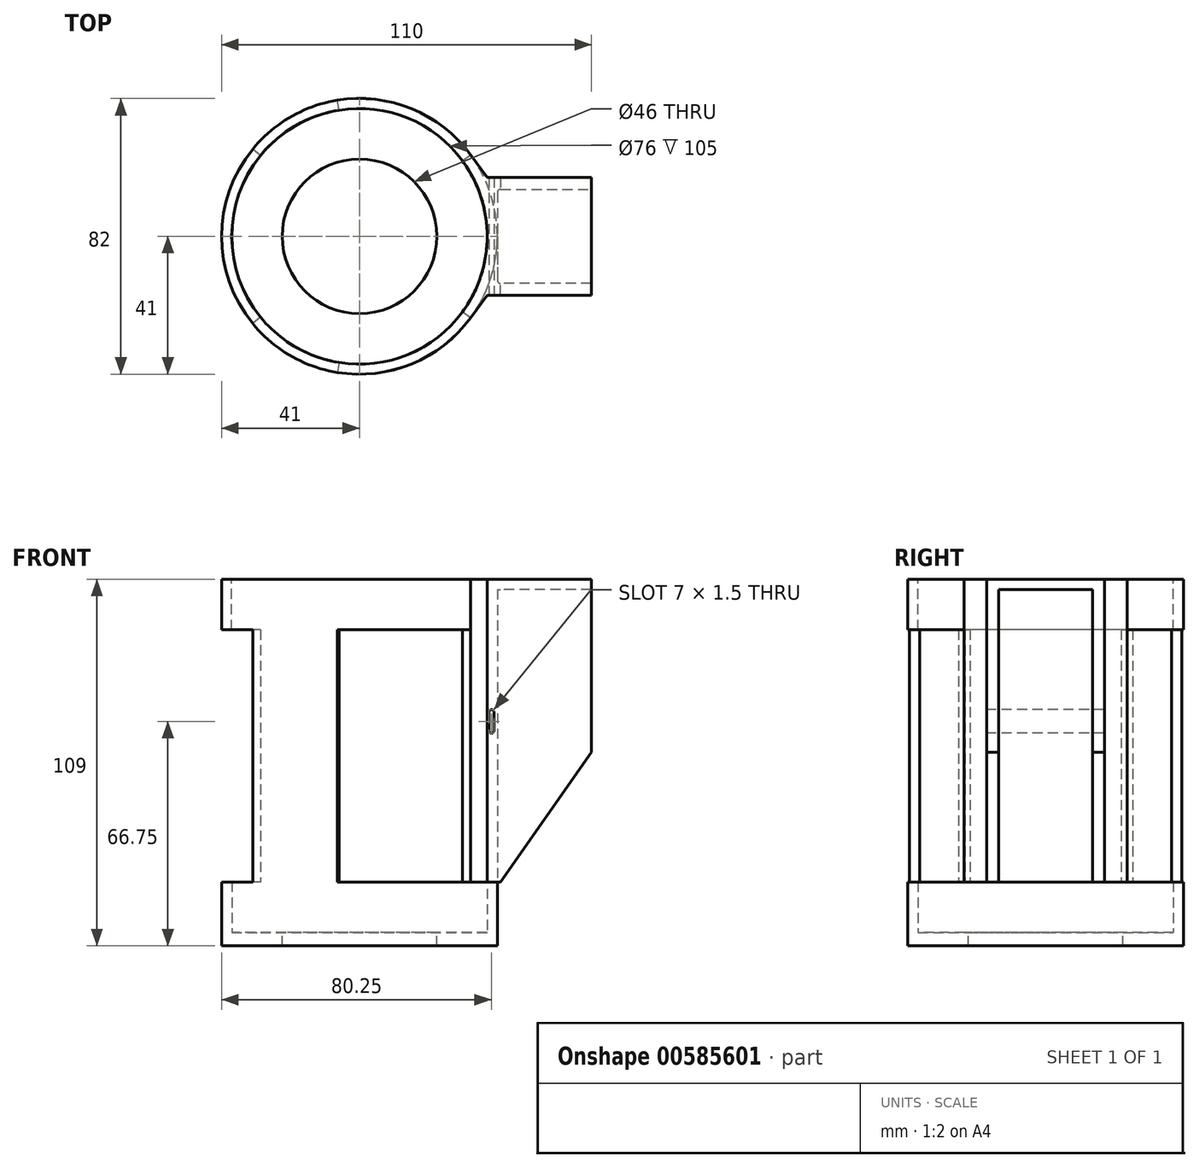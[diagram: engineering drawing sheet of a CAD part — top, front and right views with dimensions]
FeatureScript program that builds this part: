
annotation { "Feature Type Name" : "Feature", "Feature Type Description" : "" }
export const myFeature = defineFeature(function(context is Context, id is Id, definition is map)
    precondition{}
    {
        {
            var Q0;
            Q0=qCreatedBy(makeId("Top.planeOp"),FACE);
            var sketch = newSketch(context, id + "F0", { "sketchPlane" : qUnion([Q0])});
            skCircle(sketch, "E0", {"center": v(0, 0) * mm, "radius": 41 * mm});
            skCircle(sketch, "E1", {"center": v(0, 0) * mm, "radius": 23 * mm});
            skCircle(sketch, "E2", {"center": v(0, 0) * mm, "radius": 38 * mm});
            skSolve(sketch);
        }
        {
            var Q0;
            Q0=makeQuery(id+"F0.imprint","IMPRINT",FACE,{"disambiguationData":[TD([[makeQuery(id+"F0.imprint","IMPRINT",EDGE,{"derivedFrom":sQuery(id+"F0.wireOp",EDGE,"E1")}),-1.0]])]});
            var Q1;
            Q1=makeQuery(id+"F0.imprint","IMPRINT",FACE,{"disambiguationData":[TD([[makeQuery(id+"F0.imprint","IMPRINT",EDGE,{"derivedFrom":sQuery(id+"F0.wireOp",EDGE,"E0")}),1.0]])]});
            extrude(context, id + "F1", {"entities" : qUnion([Q0, Q1]), "oppositeDirection" : true, "depth" : 4 * mm, "offsetDistance" : 25 * mm});
        }
        {
            var Q0;
            Q0=makeQuery(id+"F0.imprint","IMPRINT",FACE,{"disambiguationData":[TD([[makeQuery(id+"F0.imprint","IMPRINT",EDGE,{"derivedFrom":sQuery(id+"F0.wireOp",EDGE,"E0")}),1.0]])]});
            extrude(context, id + "F2", {"entities" : qUnion([Q0]), "operationType" : NewBodyOperationType.ADD, "depth" : 15 * mm, "offsetDistance" : 25 * mm});
        }
        {
            var Q0;
            Q0=makeQuery(id+"F2.opExtrude","CAP_FACE",FACE,{"disambiguationData":[OSD([sQuery(id+"F0.wireOp",EDGE,"E0"),sQuery(id+"F0.wireOp",EDGE,"E2")])],"isStart":false});
            var sketch = newSketch(context, id + "F3", { "sketchPlane" : qUnion([Q0])});
            skLineSegment(sketch, "E3", {"start": v(38, 17.5) * mm, "end": v(0, 0) * mm});
            skLineSegment(sketch, "E4.MirrorCS", {"start": v(38, -17.5) * mm, "end": v(0, 0) * mm});
            skLineSegment(sketch, "E5", {"start": v(38, 17.5) * mm, "end": v(69, 17.5) * mm});
            skLineSegment(sketch, "E6", {"start": v(38, -17.5) * mm, "end": v(69, -17.5) * mm});
            skPoint(sketch, "E7.startSnap0", {"position": v(69, 0) * mm});
            skLineSegment(sketch, "E8", {"start": v(0, 0) * mm, "end": v(-8.31, 51.05) * mm});
            skLineSegment(sketch, "E9.MirrorCS", {"start": v(0, 0) * mm, "end": v(-40.06, 32.72) * mm});
            skLineSegment(sketch, "E10.MirrorCS", {"start": v(0, 0) * mm, "end": v(-8.31, -51.05) * mm});
            skLineSegment(sketch, "E11.MirrorCS", {"start": v(0, 0) * mm, "end": v(-40.06, -32.72) * mm});
            skPoint(sketch, "E12.visualSharp", {"position": v(41, -14) * mm});
            skPoint(sketch, "E13", {"position": v(41, 14) * mm});
            skPoint(sketch, "E14", {"position": v(69, -14) * mm});
            skPoint(sketch, "E15", {"position": v(69, 14) * mm});
            skLineSegment(sketch, "E16", {"start": v(69, -14) * mm, "end": v(42, -14) * mm});
            skLineSegment(sketch, "E17", {"start": v(41, 13) * mm, "end": v(41, -13) * mm});
            skLineSegment(sketch, "E18", {"start": v(42, 14) * mm, "end": v(69, 14) * mm});
            skLineSegment(sketch, "E19", {"start": v(69, -17.5) * mm, "end": v(69, 17.5) * mm});
            skArc(sketch, "E20.filletArc", {"start": v(41, -13) * mm, "mid": v(41.3, -13.7) * mm, "end": v(42, -14) * mm});
            skArc(sketch, "E21.filletArc", {"start": v(42, 14) * mm, "mid": v(41.3, 13.7) * mm, "end": v(41, 13) * mm});
            skLineSegment(sketch, "E22", {"start": v(38, -17.5) * mm, "end": v(33.09, -24.22) * mm});
            skLineSegment(sketch, "E23", {"start": v(38, 17.5) * mm, "end": v(33.09, 24.22) * mm});
            skLineSegment(sketch, "E24", {"start": v(33.09, -24.22) * mm, "end": v(0, 0) * mm});
            skLineSegment(sketch, "E25", {"start": v(0, 0) * mm, "end": v(33.09, 24.22) * mm});
            skSolve(sketch);
        }
        {
            var Q0;
            {var subQ0=sQuery(id+"F3.wireOp",EDGE,"E22");Q0=makeQuery(id+"F3.imprint","IMPRINT",FACE,{"disambiguationData":[TD([[makeQuery(id+"F3.imprint","IMPRINT",EDGE,{"derivedFrom":subQ0}),-1.0]])]});}
            var Q1;
            {var subQ1=sQuery(id+"F3.wireOp",EDGE,"E4.MirrorCS");var subQ3=makeQuery(id+"F2.opExtrude","CAP_EDGE",EDGE,{"disambiguationData":[OSD([sQuery(id+"F0.wireOp",EDGE,"E0")])],"isStart":false});var subQ4=makeQuery(id+"F3.imprint","INTERSECT",VERTEX,{"derivedFrom":[subQ3,subQ1]});Q1=makeQuery(id+"F3.imprint","IMPRINT",FACE,{"disambiguationData":[TD([[makeQuery(id+"F3.imprint","IMPRINT",EDGE,{"disambiguationData":[TD([[subQ4,-1.0]])],"derivedFrom":subQ3}),-1.0]])]});}
            var Q2;
            {var subQ0=sQuery(id+"F3.wireOp",EDGE,"E4.MirrorCS");var subQ1=makeQuery(id+"F2.opExtrude","CAP_EDGE",EDGE,{"disambiguationData":[OSD([sQuery(id+"F0.wireOp",EDGE,"E0")])],"isStart":false});var subQ2=makeQuery(id+"F3.imprint","INTERSECT",VERTEX,{"derivedFrom":[subQ1,subQ0]});Q2=makeQuery(id+"F3.imprint","IMPRINT",FACE,{"disambiguationData":[TD([[makeQuery(id+"F3.imprint","IMPRINT",EDGE,{"disambiguationData":[TD([[subQ2,-1.0]])],"derivedFrom":subQ0}),-1.0]])]});}
            var Q3;
            {var subQ0=sQuery(id+"F3.wireOp",EDGE,"E4.MirrorCS");var subQ1=makeQuery(id+"F2.opExtrude","CAP_EDGE",EDGE,{"disambiguationData":[OSD([sQuery(id+"F0.wireOp",EDGE,"E0")])],"isStart":false});var subQ2=makeQuery(id+"F3.imprint","INTERSECT",VERTEX,{"derivedFrom":[subQ1,subQ0]});Q3=makeQuery(id+"F3.imprint","IMPRINT",FACE,{"disambiguationData":[TD([[makeQuery(id+"F3.imprint","IMPRINT",EDGE,{"disambiguationData":[TD([[subQ2,-1.0]])],"derivedFrom":subQ0}),1.0]])]});}
            var Q4;
            {var subQ4=sQuery(id+"F3.wireOp",EDGE,"E6");Q4=makeQuery(id+"F3.imprint","IMPRINT",FACE,{"disambiguationData":[TD([[makeQuery(id+"F3.imprint","IMPRINT",EDGE,{"derivedFrom":subQ4}),1.0]])]});}
            var Q5;
            {var subQ1=sQuery(id+"F3.wireOp",EDGE,"YmZZnXxC-F3IZ-RDwF-SUU2-2qP2M3tcKqzq");var subQ3=makeQuery(id+"F2.opExtrude","CAP_EDGE",EDGE,{"disambiguationData":[OSD([sQuery(id+"F0.wireOp",EDGE,"E0")])],"isStart":false});var subQ4=makeQuery(id+"F3.imprint","INTERSECT",VERTEX,{"derivedFrom":[subQ3,subQ1]});Q5=makeQuery(id+"F3.imprint","IMPRINT",FACE,{"disambiguationData":[TD([[makeQuery(id+"F3.imprint","IMPRINT",EDGE,{"disambiguationData":[TD([[subQ4,1.0]])],"derivedFrom":subQ3}),1.0]])]});}
            var Q6;
            {var subQ5=sQuery(id+"F3.wireOp",EDGE,"E5");Q6=makeQuery(id+"F3.imprint","IMPRINT",FACE,{"disambiguationData":[TD([[makeQuery(id+"F3.imprint","IMPRINT",EDGE,{"derivedFrom":subQ5}),-1.0]])]});}
            var Q7;
            {var subQ0=sQuery(id+"F3.wireOp",EDGE,"E23");Q7=makeQuery(id+"F3.imprint","IMPRINT",FACE,{"disambiguationData":[TD([[makeQuery(id+"F3.imprint","IMPRINT",EDGE,{"derivedFrom":subQ0}),1.0]])]});}
            var Q8;
            {var subQ1=sQuery(id+"F3.wireOp",EDGE,"E3");var subQ3=makeQuery(id+"F2.opExtrude","CAP_EDGE",EDGE,{"disambiguationData":[OSD([sQuery(id+"F0.wireOp",EDGE,"E0")])],"isStart":false});var subQ4=makeQuery(id+"F3.imprint","INTERSECT",VERTEX,{"derivedFrom":[subQ3,subQ1]});Q8=makeQuery(id+"F3.imprint","IMPRINT",FACE,{"disambiguationData":[TD([[makeQuery(id+"F3.imprint","IMPRINT",EDGE,{"disambiguationData":[TD([[subQ4,1.0]])],"derivedFrom":subQ3}),-1.0]])]});}
            var Q9;
            {var subQ0=sQuery(id+"F3.wireOp",EDGE,"E3");var subQ1=makeQuery(id+"F2.opExtrude","CAP_EDGE",EDGE,{"disambiguationData":[OSD([sQuery(id+"F0.wireOp",EDGE,"E0")])],"isStart":false});var subQ2=makeQuery(id+"F3.imprint","INTERSECT",VERTEX,{"derivedFrom":[subQ1,subQ0]});Q9=makeQuery(id+"F3.imprint","IMPRINT",FACE,{"disambiguationData":[TD([[makeQuery(id+"F3.imprint","IMPRINT",EDGE,{"disambiguationData":[TD([[subQ2,-1.0]])],"derivedFrom":subQ0}),1.0]])]});}
            var Q10;
            {var subQ0=sQuery(id+"F3.wireOp",EDGE,"E3");var subQ1=makeQuery(id+"F2.opExtrude","CAP_EDGE",EDGE,{"disambiguationData":[OSD([sQuery(id+"F0.wireOp",EDGE,"E0")])],"isStart":false});var subQ2=makeQuery(id+"F3.imprint","INTERSECT",VERTEX,{"derivedFrom":[subQ1,subQ0]});Q10=makeQuery(id+"F3.imprint","IMPRINT",FACE,{"disambiguationData":[TD([[makeQuery(id+"F3.imprint","IMPRINT",EDGE,{"disambiguationData":[TD([[subQ2,-1.0]])],"derivedFrom":subQ0}),-1.0]])]});}
            var Q11;
            {var subQ0=sQuery(id+"F3.wireOp",EDGE,"E8");var subQ1=makeQuery(id+"F2.opExtrude","CAP_EDGE",EDGE,{"disambiguationData":[OSD([sQuery(id+"F0.wireOp",EDGE,"E0")])],"isStart":false});var subQ2=makeQuery(id+"F3.imprint","INTERSECT",VERTEX,{"derivedFrom":[subQ1,subQ0]});Q11=makeQuery(id+"F3.imprint","IMPRINT",FACE,{"disambiguationData":[TD([[makeQuery(id+"F3.imprint","IMPRINT",EDGE,{"disambiguationData":[TD([[subQ2,1.0]])],"derivedFrom":subQ0}),1.0]])]});}
            var Q12;
            {var subQ0=sQuery(id+"F3.wireOp",EDGE,"E10.MirrorCS");var subQ1=makeQuery(id+"F2.opExtrude","CAP_EDGE",EDGE,{"disambiguationData":[OSD([sQuery(id+"F0.wireOp",EDGE,"E0")])],"isStart":false});var subQ2=makeQuery(id+"F3.imprint","INTERSECT",VERTEX,{"derivedFrom":[subQ1,subQ0]});Q12=makeQuery(id+"F3.imprint","IMPRINT",FACE,{"disambiguationData":[TD([[makeQuery(id+"F3.imprint","IMPRINT",EDGE,{"disambiguationData":[TD([[subQ2,1.0]])],"derivedFrom":subQ0}),-1.0]])]});}
            extrude(context, id + "F4", {"entities" : qUnion([Q0, Q1, Q2, Q3, Q4, Q5, Q6, Q7, Q8, Q9, Q10, Q11, Q12]), "operationType" : NewBodyOperationType.ADD, "depth" : 90 * mm, "offsetDistance" : 25 * mm});
        }
        {
            var Q0;
            Q0=makeQuery(id+"F4.opExtrude","CAP_FACE",FACE,{"disambiguationData":[OSD([sQuery(id+"F0.wireOp",EDGE,"E2"),sQuery(id+"F3.wireOp",EDGE,"E5"),sQuery(id+"F3.wireOp",EDGE,"E6"),sQuery(id+"F3.wireOp",EDGE,"E16"),sQuery(id+"F3.wireOp",EDGE,"E17"),sQuery(id+"F3.wireOp",EDGE,"E18"),sQuery(id+"F3.wireOp",EDGE,"E19"),sQuery(id+"F3.wireOp",EDGE,"E20.filletArc"),sQuery(id+"F3.wireOp",EDGE,"E21.filletArc"),sQuery(id+"F3.wireOp",EDGE,"E22"),sQuery(id+"F3.wireOp",EDGE,"E23"),sQuery(id+"F3.wireOp",EDGE,"E24"),sQuery(id+"F3.wireOp",EDGE,"E25")])],"isStart":false});
            var sketch = newSketch(context, id + "F5", { "sketchPlane" : qUnion([Q0])});
            skCircle(sketch, "E26", {"center": v(0, 0) * mm, "radius": 38 * mm});
            skCircle(sketch, "E27", {"center": v(0, 0) * mm, "radius": 41 * mm});
            skLineSegment(sketch, "E28", {"start": v(69, 14) * mm, "end": v(69, -14) * mm});
            skSolve(sketch);
        }
        {
            var Q0;
            Q0=qSketchRegion(id+"F5",true);
            extrude(context, id + "F6", {"entities" : qUnion([Q0]), "operationType" : NewBodyOperationType.ADD, "oppositeDirection" : true, "depth" : 15 * mm, "offsetDistance" : 25 * mm});
        }
        {
            var Q0;
            Q0=makeQuery(id+"F5.imprint","IMPRINT",FACE,{"disambiguationData":[TD([[makeQuery(id+"F5.imprint","IMPRINT",EDGE,{"derivedFrom":sQuery(id+"F5.wireOp",EDGE,"E28")}),-1.0]])]});
            var Q1;
            Q1=qSketchRegion(id+"FD8Ie2CBpq4JUXR_1",true);
            extrude(context, id + "F7", {"entities" : qUnion([Q0, Q1]), "operationType" : NewBodyOperationType.ADD, "oppositeDirection" : true, "depth" : 3 * mm, "offsetDistance" : 25 * mm});
        }
        {
            var Q0;
            Q0=makeQuery(id+"F4.opExtrude","SWEPT_FACE",FACE,{"disambiguationData":[OSD([sQuery(id+"F3.wireOp",EDGE,"E6")])]});
            var sketch = newSketch(context, id + "F8", { "sketchPlane" : qUnion([Q0])});
            skLineSegment(sketch, "E29", {"start": v(38, 60) * mm, "end": v(38.5, 60) * mm});
            skLineSegment(sketch, "E30", {"start": v(38.5, 60) * mm, "end": v(38.5, 65.5) * mm});
            skLineSegment(sketch, "E31", {"start": v(38.5, 65.5) * mm, "end": v(40, 65.5) * mm});
            skLineSegment(sketch, "E32", {"start": v(40, 65.5) * mm, "end": v(40, 60) * mm});
            skLineSegment(sketch, "E33", {"start": v(40, 60) * mm, "end": v(38.5, 60) * mm});
            skCircle(sketch, "E34", {"center": v(39.25, 65.5) * mm, "radius": 0.75 * mm});
            skCircle(sketch, "E35", {"center": v(39.25, 60) * mm, "radius": 0.75 * mm});
            skLineSegment(sketch, "E36", {"start": v(38, 15) * mm, "end": v(69, 59.27) * mm});
            skLineSegment(sketch, "E37", {"start": v(38, 15) * mm, "end": v(69, 15) * mm});
            skLineSegment(sketch, "E38", {"start": v(69, 59.27) * mm, "end": v(69, 15) * mm});
            skSolve(sketch);
        }
        {
            var Q0;
            {var subQ0=sQuery(id+"F8.wireOp",EDGE,"E30");Q0=makeQuery(id+"F8.imprint","IMPRINT",FACE,{"disambiguationData":[TD([[makeQuery(id+"F8.imprint","IMPRINT",EDGE,{"derivedFrom":subQ0}),-1.0]])]});}
            var Q1;
            {var subQ0=sQuery(id+"F8.wireOp",EDGE,"E31");Q1=makeQuery(id+"F8.imprint","IMPRINT",FACE,{"disambiguationData":[TD([[makeQuery(id+"F8.imprint","IMPRINT",EDGE,{"derivedFrom":subQ0}),1.0]])]});}
            var Q2;
            {var subQ0=sQuery(id+"F8.wireOp",EDGE,"E33");Q2=makeQuery(id+"F8.imprint","IMPRINT",FACE,{"disambiguationData":[TD([[makeQuery(id+"F8.imprint","IMPRINT",EDGE,{"derivedFrom":subQ0}),1.0]])]});}
            var Q3;
            {var subQ0=sQuery(id+"F8.wireOp",EDGE,"E31");Q3=makeQuery(id+"F8.imprint","IMPRINT",FACE,{"disambiguationData":[TD([[makeQuery(id+"F8.imprint","IMPRINT",EDGE,{"derivedFrom":subQ0}),-1.0]])]});}
            var Q4;
            {var subQ0=sQuery(id+"F8.wireOp",EDGE,"E33");Q4=makeQuery(id+"F8.imprint","IMPRINT",FACE,{"disambiguationData":[TD([[makeQuery(id+"F8.imprint","IMPRINT",EDGE,{"derivedFrom":subQ0}),-1.0]])]});}
            var Q5;
            Q5=makeQuery(id+"F4.opExtrude","SWEPT_FACE",FACE,{"disambiguationData":[OSD([sQuery(id+"F3.wireOp",EDGE,"E5")])]});
            extrude(context, id + "F9", {"entities" : qUnion([Q0, Q1, Q2, Q3, Q4]), "operationType" : NewBodyOperationType.REMOVE, "endBound" : BoundingType.UP_TO_SURFACE, "oppositeDirection" : true, "depth" : 25 * mm, "endBoundEntityFace" : qUnion([Q5]), "offsetDistance" : 25 * mm});
        }
        {
            var Q0;
            Q0=makeQuery(id+"F4.opExtrude","SWEPT_FACE",FACE,{"disambiguationData":[OSD([sQuery(id+"F3.wireOp",EDGE,"E16")])]});
            var sketch = newSketch(context, id + "F10", { "sketchPlane" : qUnion([Q0])});
            skLineSegment(sketch, "E39", {"start": v(-42, 15) * mm, "end": v(-69, 15) * mm});
            skLineSegment(sketch, "E40", {"start": v(-69, 15) * mm, "end": v(-69, 53.56) * mm});
            skLineSegment(sketch, "E41", {"start": v(-69, 53.56) * mm, "end": v(-42, 15) * mm});
            skSolve(sketch);
        }
        {
            var Q0;
            Q0=makeQuery(id+"F10.imprint","IMPRINT",FACE,{"disambiguationData":[TD([[makeQuery(id+"F10.imprint","IMPRINT",EDGE,{"derivedFrom":sQuery(id+"F10.wireOp",EDGE,"E39")}),1.0]])]});
            extrude(context, id + "F11", {"entities" : qUnion([Q0]), "operationType" : NewBodyOperationType.REMOVE, "oppositeDirection" : true, "depth" : 25 * mm, "offsetDistance" : 25 * mm});
        }
        {
            var Q0;
            Q0=makeQuery(id+"F10.imprint","IMPRINT",FACE,{"disambiguationData":[TD([[makeQuery(id+"F10.imprint","IMPRINT",EDGE,{"derivedFrom":sQuery(id+"F10.wireOp",EDGE,"E39")}),1.0]])]});
            extrude(context, id + "F12", {"entities" : qUnion([Q0]), "operationType" : NewBodyOperationType.REMOVE, "depth" : 35.5 * mm, "offsetDistance" : 25 * mm});
        }
    });
